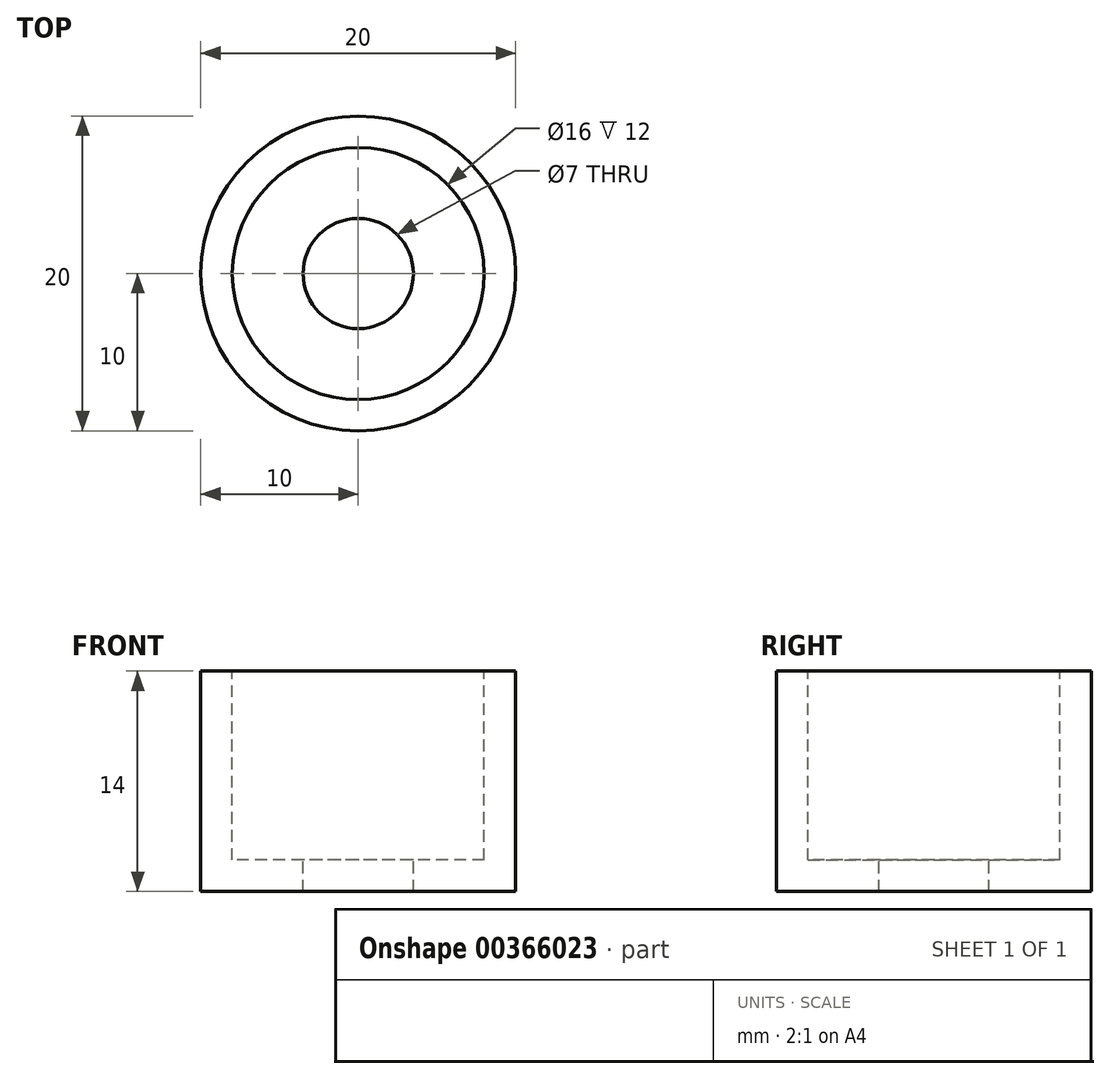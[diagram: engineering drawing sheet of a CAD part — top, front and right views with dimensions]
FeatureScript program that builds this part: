
annotation { "Feature Type Name" : "Feature", "Feature Type Description" : "" }
export const myFeature = defineFeature(function(context is Context, id is Id, definition is map)
    precondition{}
    {
        {
            var Q0;
            Q0=qCreatedBy(makeId("Top.planeOp"),FACE);
            var sketch = newSketch(context, id + "F0", { "sketchPlane" : qUnion([Q0])});
            skCircle(sketch, "E0", {"center": v(0, 0) * mm, "radius": 10 * mm});
            skSolve(sketch);
        }
        {
            var Q0;
            Q0=makeQuery(id+"F0.imprint","IMPRINT",FACE,{"disambiguationData":[TD([[makeQuery(id+"F0.imprint","IMPRINT",EDGE,{"derivedFrom":sQuery(id+"F0.wireOp",EDGE,"E0")}),1.0]])]});
            extrude(context, id + "F1", {"entities" : qUnion([Q0]), "depth" : 14 * mm});
        }
        {
            var Q0;
            Q0=makeQuery(id+"F1.opExtrude","CAP_FACE",FACE,{"disambiguationData":[OSD([sQuery(id+"F0.wireOp",EDGE,"E0")])],"isStart":false});
            cPlane(context, id + "F2", {"entities" : qUnion([Q0]), "cplaneType" : CPlaneType.OFFSET, "offset" : 0 * mm, "width" : 150 * mm, "height" : 150 * mm});
        }
        {
            var Q0;
            Q0=qCreatedBy(id+"F2.planeOp",FACE);
            var sketch = newSketch(context, id + "F3", { "sketchPlane" : qUnion([Q0])});
            skPoint(sketch, "E1", {"position": v(0, 0) * mm});
            skSolve(sketch);
        }
        {
            var Q0;
            Q0=qCreatedBy(id+"F2.planeOp",FACE);
            var sketch = newSketch(context, id + "F4", { "sketchPlane" : qUnion([Q0])});
            skCircle(sketch, "E2", {"center": v(0, 0) * mm, "radius": 8 * mm});
            skSolve(sketch);
        }
        {
            var Q0;
            Q0=makeQuery(id+"F4.imprint","IMPRINT",FACE,{"disambiguationData":[TD([[makeQuery(id+"F4.imprint","IMPRINT",EDGE,{"derivedFrom":sQuery(id+"F4.wireOp",EDGE,"E2")}),1.0]])]});
            extrude(context, id + "F5", {"entities" : qUnion([Q0]), "operationType" : NewBodyOperationType.REMOVE, "oppositeDirection" : true, "depth" : 12 * mm});
        }
        {
            var Q0;
            Q0=sQuery(id+"F3.wireOp",VERTEX,"E1");
            var Q1;
            Q1=makeQuery(id+"F1.opExtrude","SWEPT_BODY",BODY,{"disambiguationData":[OSD([sQuery(id+"F0.wireOp",EDGE,"E0")])]});
            hole(context, id + "F6", {"style" : HoleStyle.SIMPLE, "endStyle" : HoleEndStyle.THROUGH, "holeDiameter" : 7 * mm, "isTappedThrough" : true, "tappedDepth" : 2 * mm, "tapClearance" : 3, "startFromSketch" : true, "locations" : qUnion([Q0]), "scope" : qUnion([Q1])});
        }
    });
